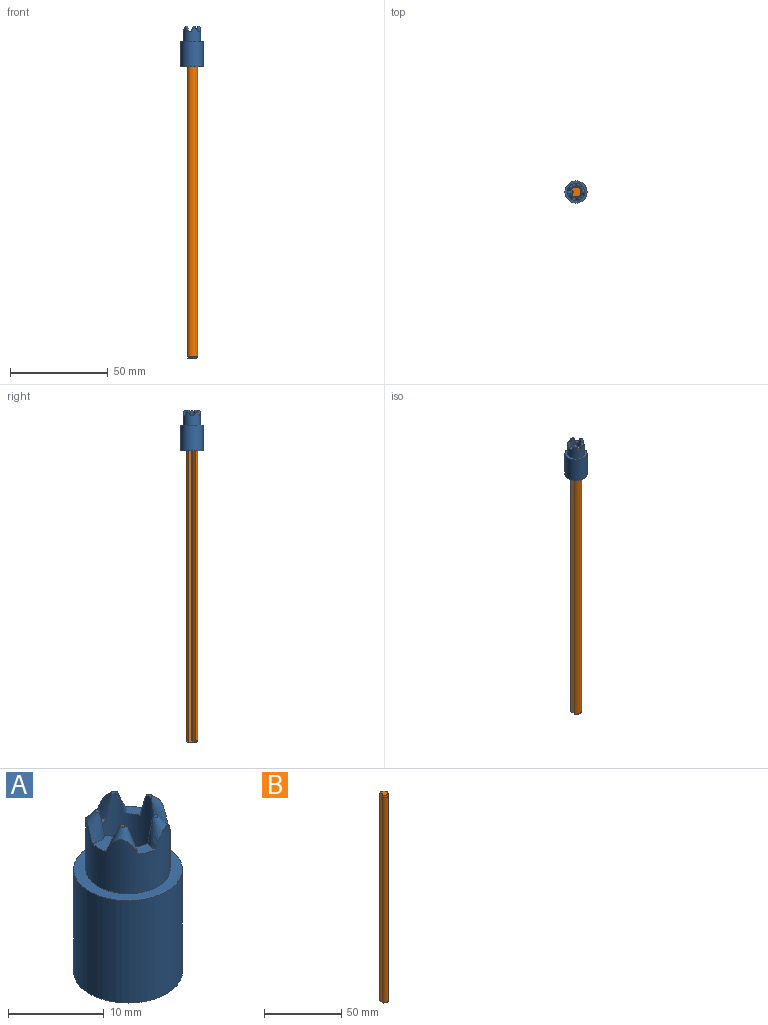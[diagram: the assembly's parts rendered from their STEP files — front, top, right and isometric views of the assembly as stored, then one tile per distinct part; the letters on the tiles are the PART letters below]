
ASSEMBLY  parts=2 mates=1
PART A: 25 faces, bbox 11.7x11.7x21.3 mm
  f0: cone r=1.8mm half-angle=24.8deg, axis (0.34,0,-0.94), area 9mm2, adj f1,f2,f3,f4,f21
  f1: plane 0.97x0.71mm, normal (0,0,1), area 0.2mm2, adj f0,f2
  f2: cylinder r=3.06mm len=20.85mm, axis (0,0,-1), area 308.4mm2, adj f0,f1,f4,f5,f6,f7,f8,f9
  f3: cylinder r=4.4mm len=8.8mm, axis (0,0,-1), area 159.2mm2, adj f0,f4,f6,f7,f11,f12,f16,f17
  f4: plane 2.32x2.22mm, normal (0,0,1), area 2.2mm2, adj f0,f2,f3,f6
  f5: plane 0.97x0.81mm, normal (0,0,1), area 0.2mm2, adj f2,f6
  f6: cone r=1.8mm half-angle=24.8deg, axis (0.11,0.33,-0.94), area 9mm2, adj f2,f3,f4,f5,f7
  f7: plane 2.2x1.91mm, normal (0,0,1), area 2.2mm2, adj f2,f3,f6,f11
  f8: plane 0.63x0.58mm, normal (0,0,1), area 0.2mm2, adj f2,f11
  f9: cylinder r=0.15mm len=20.77mm, axis (0,0,-1), area 4mm2, adj f2,f10,f11,f23
  f10: plane 20.17x0.68mm, normal (0.71,0.71,0), area 17.7mm2, adj f9,f11,f12,f20,f23
  f11: cone r=1.8mm half-angle=24.8deg, axis (-0.28,0.2,-0.94), area 9.8mm2, adj f2,f3,f7,f8,f9,f10,f12
  f12: plane 2.7x2.17mm, normal (0,0,1), area 4.4mm2, adj f3,f10,f11,f14,f16,f20
  f13: plane 0.63x0.58mm, normal (0,0,1), area 0.2mm2, adj f2,f16
  f14: plane 20.17x0.68mm, normal (0.71,-0.71,0), area 17.7mm2, adj f12,f15,f16,f20,f23
  f15: cylinder r=0.15mm len=20.77mm, axis (0,0,-1), area 4mm2, adj f2,f14,f16,f23
  f16: cone r=1.8mm half-angle=24.8deg, axis (-0.28,-0.2,-0.94), area 9.8mm2, adj f2,f3,f12,f13,f14,f15,f17
  f17: plane 2.2x1.91mm, normal (0,0,1), area 2.2mm2, adj f2,f3,f16,f18
  f18: cone r=1.8mm half-angle=24.8deg, axis (0.11,-0.33,-0.94), area 9mm2, adj f2,f3,f17,f19,f21
  f19: plane 0.97x0.81mm, normal (0,0,1), area 0.2mm2, adj f2,f18
  f20: cylinder r=0.9mm len=17.97mm, axis (0,0,-1), area 25.4mm2, adj f10,f12,f14,f23
  f21: plane 2.32x2.22mm, normal (0,0,1), area 2.2mm2, adj f0,f2,f3,f18
  f22: cylinder r=5.68mm len=13.05mm, axis (0,0,1), area 465.3mm2, adj f23,f24
  f23: plane 11.35x11.35mm, normal (0,0,-1), area 74.2mm2, adj f2,f9,f10,f14,f15,f20,f22
  f24: plane 11.35x11.35mm, normal (0,0,1), area 40.4mm2, adj f3,f22
PART B: 8 faces, bbox 5.6x5.9x165 mm
  f0: plane 165.02x1.36mm, normal (-0.71,0.71,0), area 311.6mm2, adj f1,f3,f4,f5,f6,f7
  f1: cylinder r=2.95mm len=162.9mm, axis (0,0,-1), area 2482.7mm2, adj f0,f2,f6,f7
  f2: plane 165.02x1.36mm, normal (-0.71,-0.71,0), area 311.6mm2, adj f1,f3,f4,f5,f6,f7
  f3: cylinder r=0.3mm len=165mm, axis (0,0,-1), area 77.8mm2, adj f0,f2,f4,f5
  f4: plane 5.09x4.75mm, normal (0,0,1), area 18.2mm2, adj f0,f2,f3,f7
  f5: plane 4.69x4.41mm, normal (0,0,-1), area 15.6mm2, adj f0,f2,f3,f6
  f6: cone r=2.95mm half-angle=45deg, axis (0,0,1), area 11.7mm2, adj f0,f1,f2,f5
  f7: cone r=2.54mm half-angle=15deg, axis (0,0,-1), area 22.2mm2, adj f0,f1,f2,f4
PLACE A at identity fixed
PLACE B t=(0,0,-162.15)mm
MATE fastened B.f1 <-> A.f2  axis (0,0,1) through (0,0,2.85)mm
